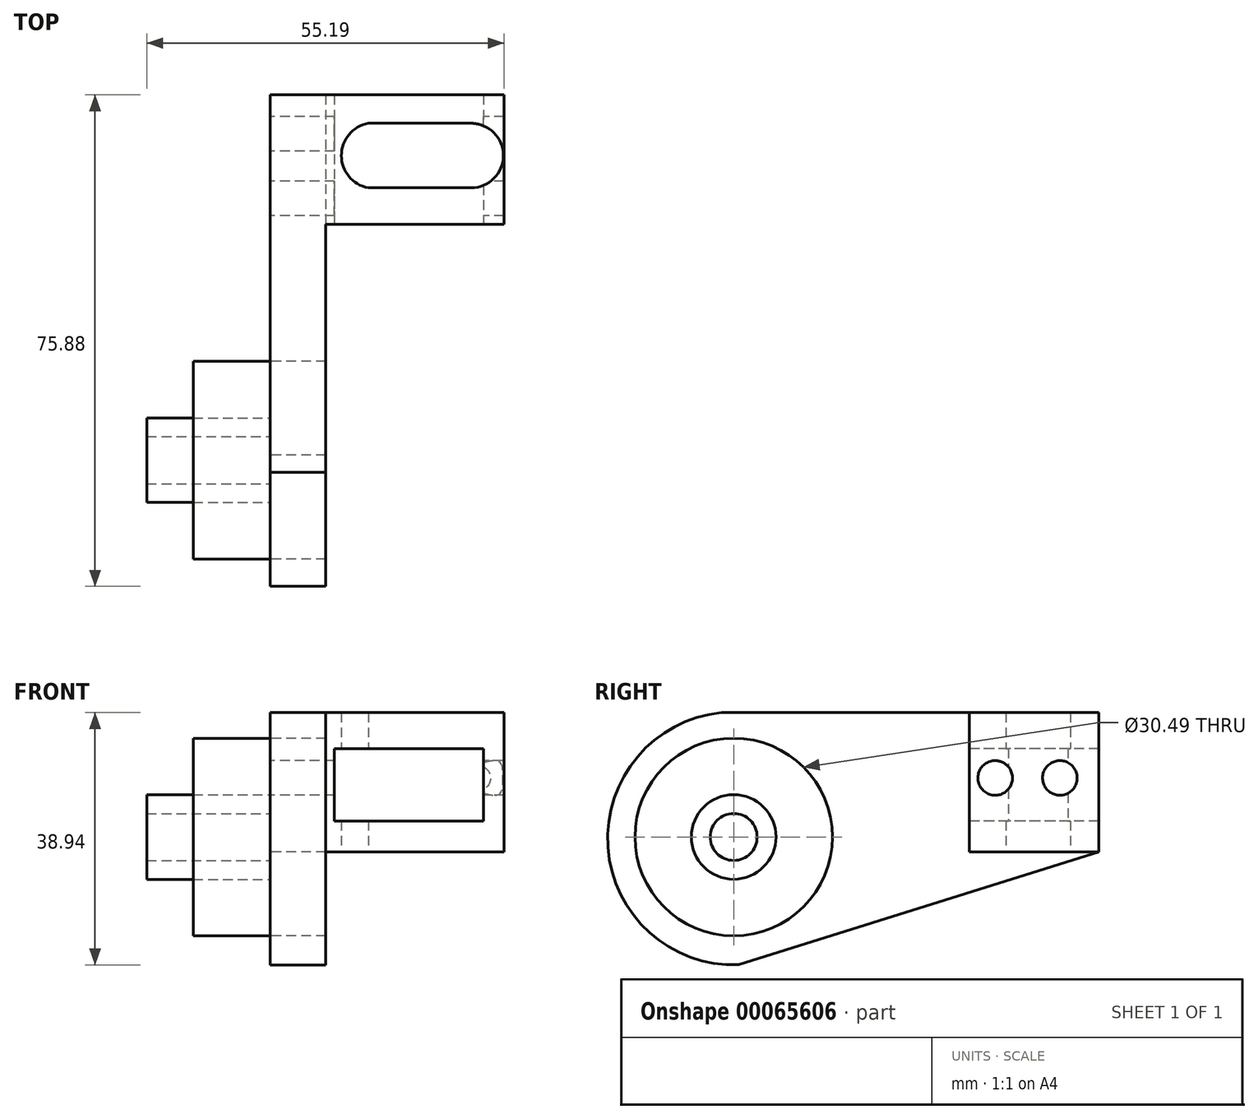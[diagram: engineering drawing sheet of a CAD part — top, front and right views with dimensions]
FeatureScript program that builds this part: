
annotation { "Feature Type Name" : "Feature", "Feature Type Description" : "" }
export const myFeature = defineFeature(function(context is Context, id is Id, definition is map)
    precondition{}
    {
        {
            var Q0;
            Q0=qCreatedBy(makeId("Right.planeOp"),FACE);
            var sketch = newSketch(context, id + "F0", { "sketchPlane" : qUnion([Q0])});
            skCircle(sketch, "E0", {"center": v(-20.8, 2.33) * mm, "radius": 3.62 * mm});
            skCircle(sketch, "E1", {"center": v(-20.8, 2.33) * mm, "radius": 6.53 * mm});
            skCircle(sketch, "E2", {"center": v(-20.8, 2.33) * mm, "radius": 15.25 * mm});
            skArc(sketch, "E3", {"start": v(-22.67, 21.53) * mm, "mid": v(-40.23, 0.77) * mm, "end": v(-20, -17.4) * mm});
            skLineSegment(sketch, "E4", {"start": v(35.6, 21.53) * mm, "end": v(35.6, 0) * mm});
            skLineSegment(sketch, "E5", {"start": v(35.6, 0) * mm, "end": v(15.6, 0) * mm});
            skLineSegment(sketch, "E6", {"start": v(15.6, 0) * mm, "end": v(15.6, 21.53) * mm});
            skLineSegment(sketch, "E7", {"start": v(15.6, 21.53) * mm, "end": v(15.6, 13.4) * mm});
            skLineSegment(sketch, "E8", {"start": v(-20, -17.4) * mm, "end": v(35.6, 0) * mm});
            skLineSegment(sketch, "E9", {"start": v(-22.67, 21.53) * mm, "end": v(15.6, 21.53) * mm});
            skLineSegment(sketch, "E10", {"start": v(15.6, 21.53) * mm, "end": v(35.6, 21.53) * mm});
            skCircle(sketch, "E11", {"center": v(19.6, 11.45) * mm, "radius": 2.67 * mm});
            skCircle(sketch, "E12", {"center": v(29.6, 11.45) * mm, "radius": 2.67 * mm});
            skLineSegment(sketch, "E13", {"start": v(29.57, 14.04) * mm, "end": v(29.6, 8.77) * mm});
            skLineSegment(sketch, "E14", {"start": v(16.92, 11.45) * mm, "end": v(22.27, 11.45) * mm});
            skLineSegment(sketch, "E15", {"start": v(19.7, 14.12) * mm, "end": v(19.7, 8.78) * mm});
            skLineSegment(sketch, "E16", {"start": v(32.27, 11.45) * mm, "end": v(26.92, 11.45) * mm});
            skSolve(sketch);
        }
        {
            var Q0;
            Q0=makeQuery(id+"F0.imprint","IMPRINT",FACE,{"disambiguationData":[TD([[makeQuery(id+"F0.imprint","IMPRINT",EDGE,{"derivedFrom":sQuery(id+"F0.wireOp",EDGE,"E0")}),-1.0]])]});
            extrude(context, id + "F1", {"entities" : qUnion([Q0]), "oppositeDirection" : true, "depth" : 19.06 * mm});
        }
        {
            var Q0;
            Q0=makeQuery(id+"F0.imprint","IMPRINT",FACE,{"disambiguationData":[TD([[makeQuery(id+"F0.imprint","IMPRINT",EDGE,{"derivedFrom":sQuery(id+"F0.wireOp",EDGE,"E1")}),-1.0]])]});
            extrude(context, id + "F2", {"entities" : qUnion([Q0]), "oppositeDirection" : true, "depth" : 11.9 * mm});
        }
        {
            var Q0;
            Q0=makeQuery(id+"F0.imprint","IMPRINT",FACE,{"disambiguationData":[TD([[makeQuery(id+"F0.imprint","IMPRINT",EDGE,{"derivedFrom":sQuery(id+"F0.wireOp",EDGE,"E2")}),-1.0]])]});
            extrude(context, id + "F3", {"entities" : qUnion([Q0]), "depth" : 8.6 * mm});
        }
        {
            var Q0;
            Q0=makeQuery(id+"F0.imprint","IMPRINT",FACE,{"disambiguationData":[TD([[makeQuery(id+"F0.imprint","IMPRINT",EDGE,{"derivedFrom":sQuery(id+"F0.wireOp",EDGE,"E4")}),-1.0]])]});
            extrude(context, id + "F4", {"entities" : qUnion([Q0]), "operationType" : NewBodyOperationType.ADD, "depth" : 36.13 * mm});
        }
        {
            var Q0;
            Q0=qCreatedBy(makeId("Top.planeOp"),FACE);
            var sketch = newSketch(context, id + "F5", { "sketchPlane" : qUnion([Q0])});
            skLineSegment(sketch, "E17", {"start": v(31.04, 31.21) * mm, "end": v(15.15, 31.21) * mm});
            skLineSegment(sketch, "E18", {"start": v(31.04, 21.26) * mm, "end": v(15.15, 21.26) * mm});
            skArc(sketch, "E19", {"start": v(31.04, 21.26) * mm, "mid": v(36.02, 26.24) * mm, "end": v(31.04, 31.21) * mm});
            skArc(sketch, "E20", {"start": v(15.15, 31.21) * mm, "mid": v(11, 26.24) * mm, "end": v(15.15, 21.26) * mm});
            skSolve(sketch);
        }
        {
            var Q0;
            Q0=makeQuery(id+"F5.imprint","IMPRINT",FACE,{"disambiguationData":[TD([[makeQuery(id+"F5.imprint","IMPRINT",EDGE,{"derivedFrom":sQuery(id+"F5.wireOp",EDGE,"E17")}),1.0]])]});
            extrude(context, id + "F6", {"entities" : qUnion([Q0]), "operationType" : NewBodyOperationType.REMOVE, "depth" : 22.59 * mm});
        }
        {
            var Q0;
            Q0=makeQuery(id+"F4.opExtrude","SWEPT_FACE",FACE,{"disambiguationData":[OSD([sQuery(id+"F0.wireOp",EDGE,"E6"),sQuery(id+"F0.wireOp",EDGE,"E7")])]});
            var sketch = newSketch(context, id + "F7", { "sketchPlane" : qUnion([Q0])});
            skLineSegment(sketch, "E21.bottom", {"start": v(32.93, 15.98) * mm, "end": v(9.92, 15.98) * mm});
            skLineSegment(sketch, "E21.top", {"start": v(32.93, 4.82) * mm, "end": v(9.92, 4.82) * mm});
            skLineSegment(sketch, "E21.left", {"start": v(32.93, 15.98) * mm, "end": v(32.93, 4.82) * mm});
            skLineSegment(sketch, "E21.right", {"start": v(9.92, 15.98) * mm, "end": v(9.92, 4.82) * mm});
            skSolve(sketch);
        }
        {
            var Q0;
            Q0=makeQuery(id+"F7.imprint","IMPRINT",FACE,{"disambiguationData":[TD([[makeQuery(id+"F7.imprint","IMPRINT",EDGE,{"derivedFrom":sQuery(id+"F7.wireOp",EDGE,"E21.bottom")}),1.0]])]});
            extrude(context, id + "F8", {"entities" : qUnion([Q0]), "operationType" : NewBodyOperationType.REMOVE, "oppositeDirection" : true, "depth" : 25 * mm});
        }
    });
